# Revit family: Фильтр для горячей воды 0554
name_source: partatom
category: Rohrzubehör
units: mm (PartAtom-declared; Revit-internal decimal feet)

## family parameters
Arbeitsebenenbasiert = Nein
Beim Laden mit Abzugskörper schneiden = Nein
Bemaßung runder Anschluss = Durchmesser verwenden
Gemeinsam genutzt = Nein
Immer vertikal = Ja
OmniClass-Nummer = 23.65.55.14
OmniClass-Titel = Valves for Liquid Services
Teiletyp = Unterbricht

## types (1)
- Фильтр для горячей воды 0554
    D01 = 25.5 mm
    D02 = 22.75 mm  [stored 0.0746391 ft]
    H01 = 24 mm  [stored 0.0787402 ft]
    H02 = 45.5 mm  [stored 0.149278 ft]
    H03 = 67.5 mm
    H04 = 151 mm
    Hersteller = HERZ Armaturen Ges.m.b.H.
    R01 = 12.5 mm  [stored 0.0410105 ft]
    R02 = 8 mm  [stored 0.0262467 ft]
    SCTWCODE = 02;00;02
    SCTWSEQ = FI;SBT_TYP_FI="FI";2
    SC_NennweiteBerechnet = 0
    T01 = 1 mm  [stored 0.00328084 ft]
    URL = www.herz-armaturen.ru
    VRS01 = 10 mm  [stored 0.0328084 ft]
    Vorgabe-Ansicht = 0 mm  [stored 0 ft]
    W01 = 89.00°
    W02 = 88.00°
    Исполнение = HERZ-фильтр для воды устанавливается на вводе в здание для предотвращения попадания загрязнений в питьевую воду.
    Корпус = латунь, CW617N
    Макс. рабочая температура = 60 °C
    Макс. рабочее давление = 1600000.0 Pa
    Модель = Фильтр для горячей воды с корпусом из латуни и чашей из трогамида.
    Примечание = В соответствии со статьей 33 Регламента REACH (Registration; Evaluation; Authorisation; Restriction of Chemicals) (EC № 1907/2006) мы обязаны указать, что свинец внесен в список SVHC (Substances of Very High Concern - вещества очень высокой важности) и весовой процент свинца во всех латунных компонентах заводского изготовления в наших изделиях, превышает 0,1 % (w/w) (CAS: 7439-92-1 / EINECS: 231-100-4).
Поскольку свинец является легирующим компонентом сплава, прямое негативное влияние исключается, и поэтому дополнительной информации о безопасном использовании не требуется.
    Среда = Питьевая вода
    Фильтрующий элемент = нержавеющая сталь, тонкость фильтрации 100 мкм
    Чаша = пластик, трогамид

note: [stored X ft] marks values corroborated as IEEE doubles in the binary element streams (Revit-internal decimal feet)
